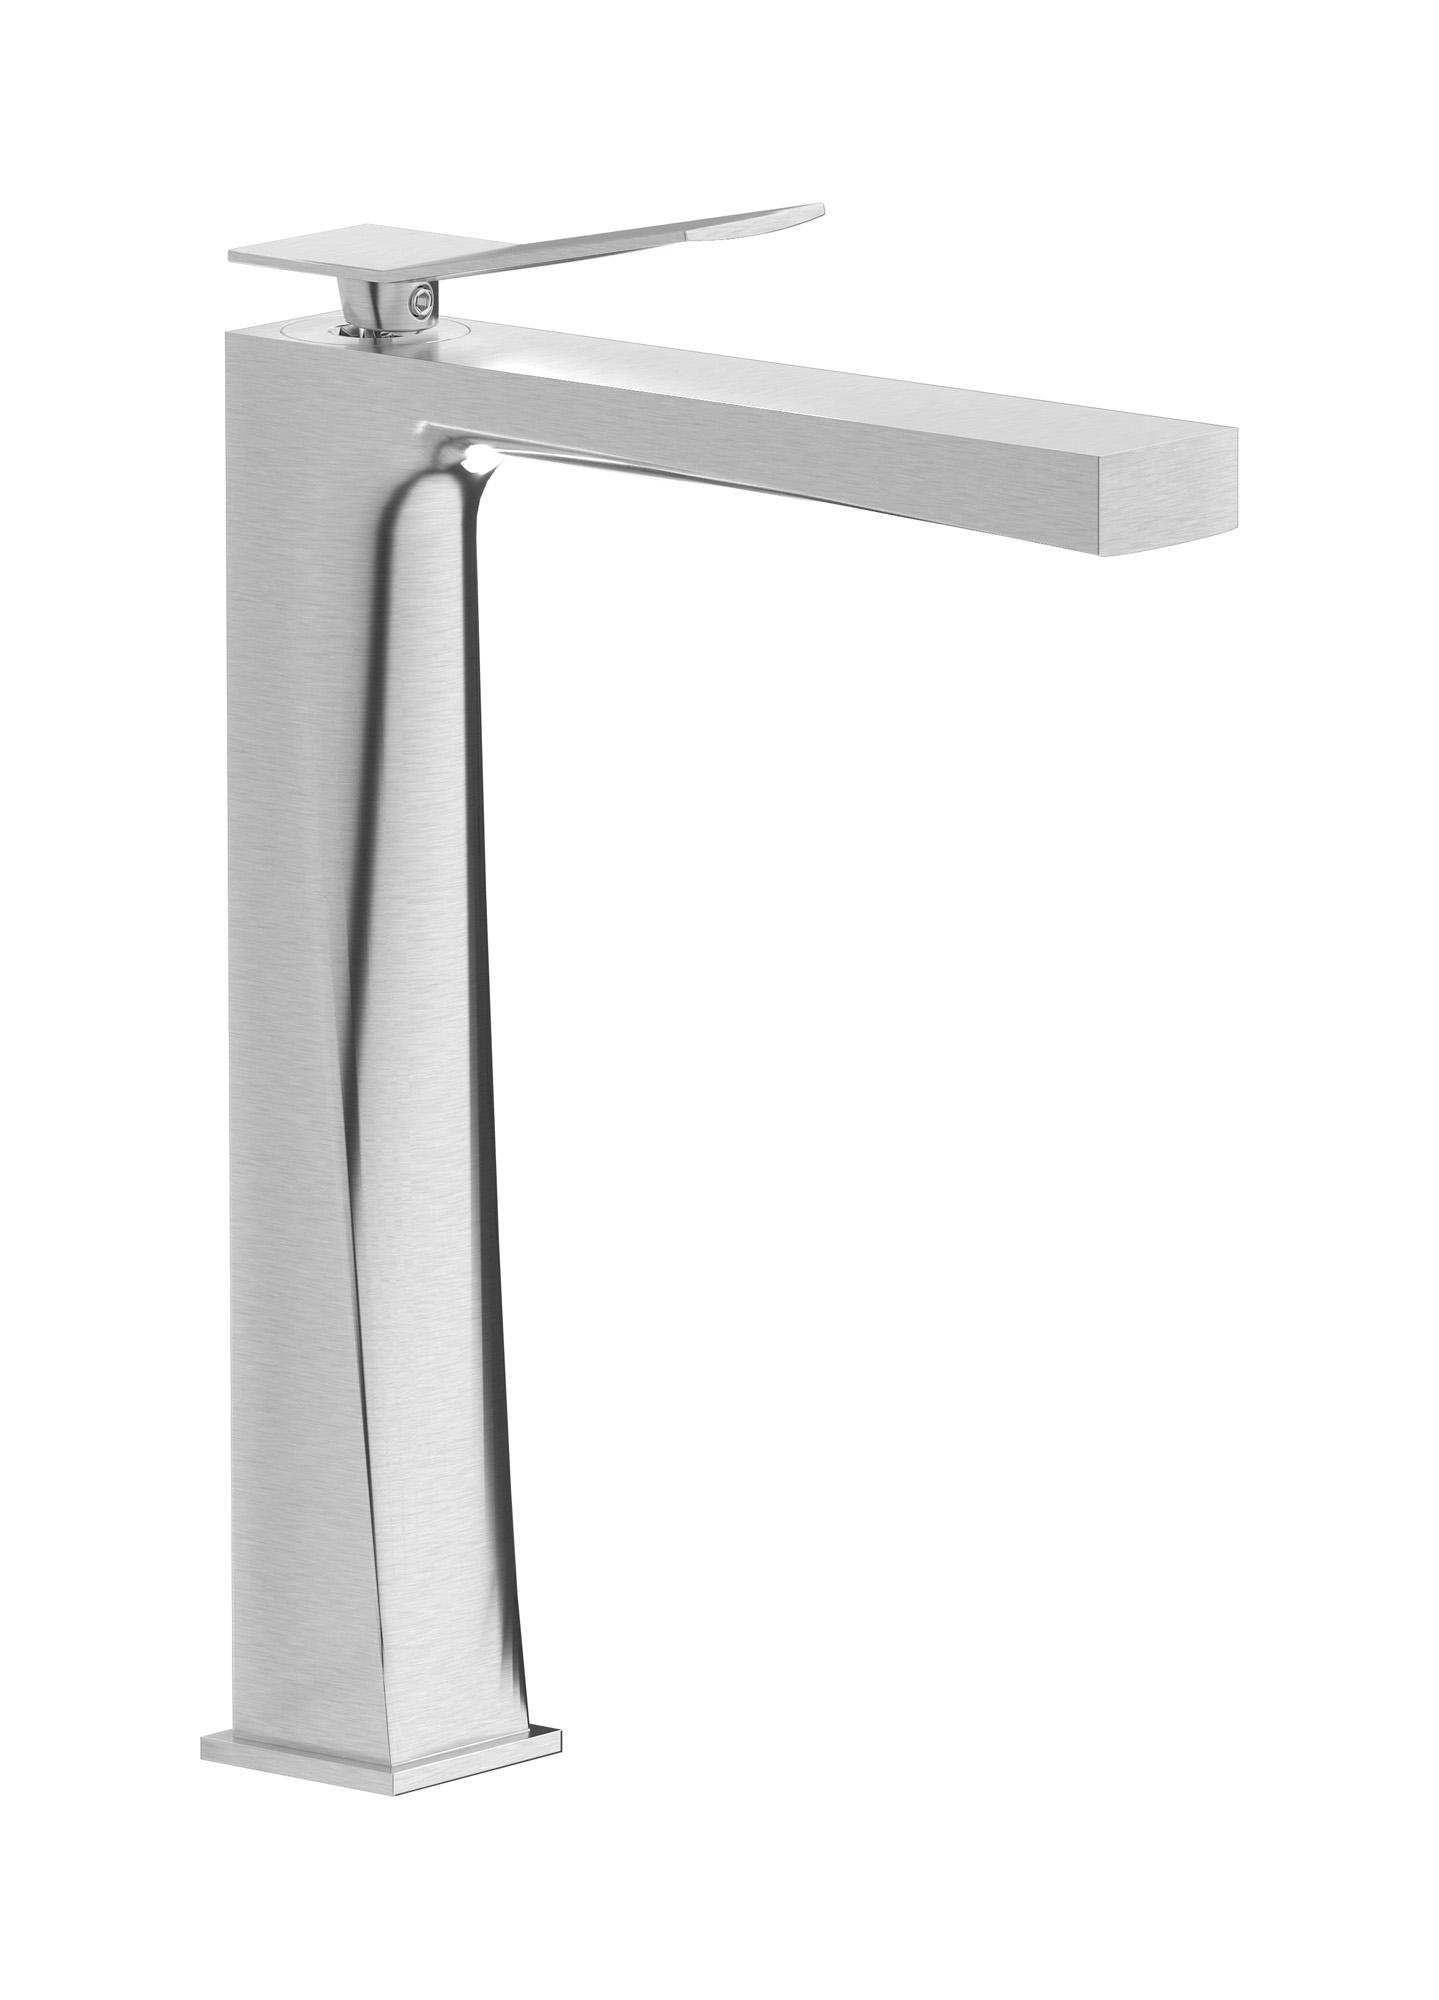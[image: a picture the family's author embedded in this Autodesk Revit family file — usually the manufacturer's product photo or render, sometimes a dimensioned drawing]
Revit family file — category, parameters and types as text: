
# Revit family: WA202
name_source: partatom
category: Apparecchi idraulici
units: mm (PartAtom-declared; Revit-internal decimal feet)

## family parameters
Basato su piano di lavoro = No
Condiviso = No
Mantieni orientamento annotazione = No
Numero OmniClass = 23.45.55.17
Punto di calcolo locali = No
Quota connettore circolare = Usa diametro
Sempre verticale = Sì
Taglio con vuoti quando caricato = No
Tipo di parte = Normale
Titolo OmniClass = Mixing Faucets

## types (12) — shared parameters
Cold water inlet = 10 mm  [stored 0.0328084 ft]
Commenti sul tipo = Washbasin mixer
Connessione CW = No
Connessione HW = No
Connessione di scarico = No
Connessione di ventilazione = No
Descrizione = Tall monohole washbasin mixer complete with drain
Hot water inlet = 10 mm  [stored 0.0328084 ft]
Produttore = IB Rubinetterie S.p.A.
URL = https://www.weareib.it
zero-valued in all types: Prospetto di default

## per-type parameters (varying)
| type | Finishes surface | Immagine tipo | Modello |
| Chrome | IB_Chrome | WA202CC.jpg | WA202CC |
| Brushed nickel | IB_Brushed nickel | WA202SS.jpg | WA202SS |
| Matt white | IB_matt white | WA202BO.jpg | WA202BO |
| Matt black | IB_matt black | WA202NP.jpg | WA202NP |
| Black chrome | IB_Black chrome | WA202CF.jpg | WA202CF |
| Brushed black chrome | IB_Brushed black chrome | WA202CS.jpg | WA202CS |
| Pale gold | IB_Pale gold | WA202II.jpg | WA202II |
| Brushed pale gold | IB_brushed pale gold | WA202IS.jpg | WA202IS |
| Rose gold | IB_Rose gold | WA202RS.jpg | WA202RS |
| Brushed rose gold | IB_Brushed rose gold | WA202SR.jpg | WA202SR |
| Gold | IB_gold | WA202OO.jpg | WA202OO |
| Brushed gold | IB_brushed gold | WA202OS.jpg | WA202OS |

note: [stored X ft] marks values corroborated as IEEE doubles in the binary element streams (Revit-internal decimal feet)
